# Revit family: Gira_0286600
name_source: partatom
category: Electrical Fixtures
revit_build: Autodesk Revit 2017 (Build: 20160225_1515(x64)
units: mm (PartAtom-declared; Revit-internal decimal feet)

## family parameters
Cut with Voids When Loaded = No
Host = Face
Maintain Annotation Orientation = No
Part Type = Normal
Room Calculation Point = No
Round Connector Dimension = Use Diameter
Shared = No

## types (1)
- Rocker sym.bell System 55 stainl.steel
    Available = No
    BIM (1) = https://media.stage.bim.site und Tasten.rfa?public/gira/36a6b08/Sys55_Abdeckung_Schalten und Tasten.rfa
    Category = Control element/cover plate for domestic switching devices
    Colour = Stainless steel
    Data sheet (1) = https://katalog.gira.de
    Default Elevation = 1219 mm
    Description = Rock.sym.bell Sys55 SST,Rocker with symbol,Bell,Stainless steel,
    GTIN = 4010337021698
    HAN = 0286600
    Halogen free = No
    HeinzeBIM = https://bimportal.heinze.de
    Imprint/indication = Symbol "Klingel" (*de-DE)
    Manufacturer = Gira
    Manufacturer URL = https://www.gira.de
    Material = Metal
    Material quality = Stainless steel
    Model = Single rocker
    Monitoring window/light outlet = Yes
    Name = Rocker sym.bell System 55 stainl.steel
    Scannable symbol / barrier free = No
    Suitable for degree of protection (IP) = IP20
    Suitable for touch sensor connector for bus system = No
    Surface protection = Other
    Type of fastening = Clamp mounting
    URL = http://katalog.gira.de
    Utilization = Switch/push button
    With exchangeable lens/symbol = No
    With label area = No

## geometry (parser evidence)
native form markers: Sweep x4
no freeform markers — native parametric forms only
